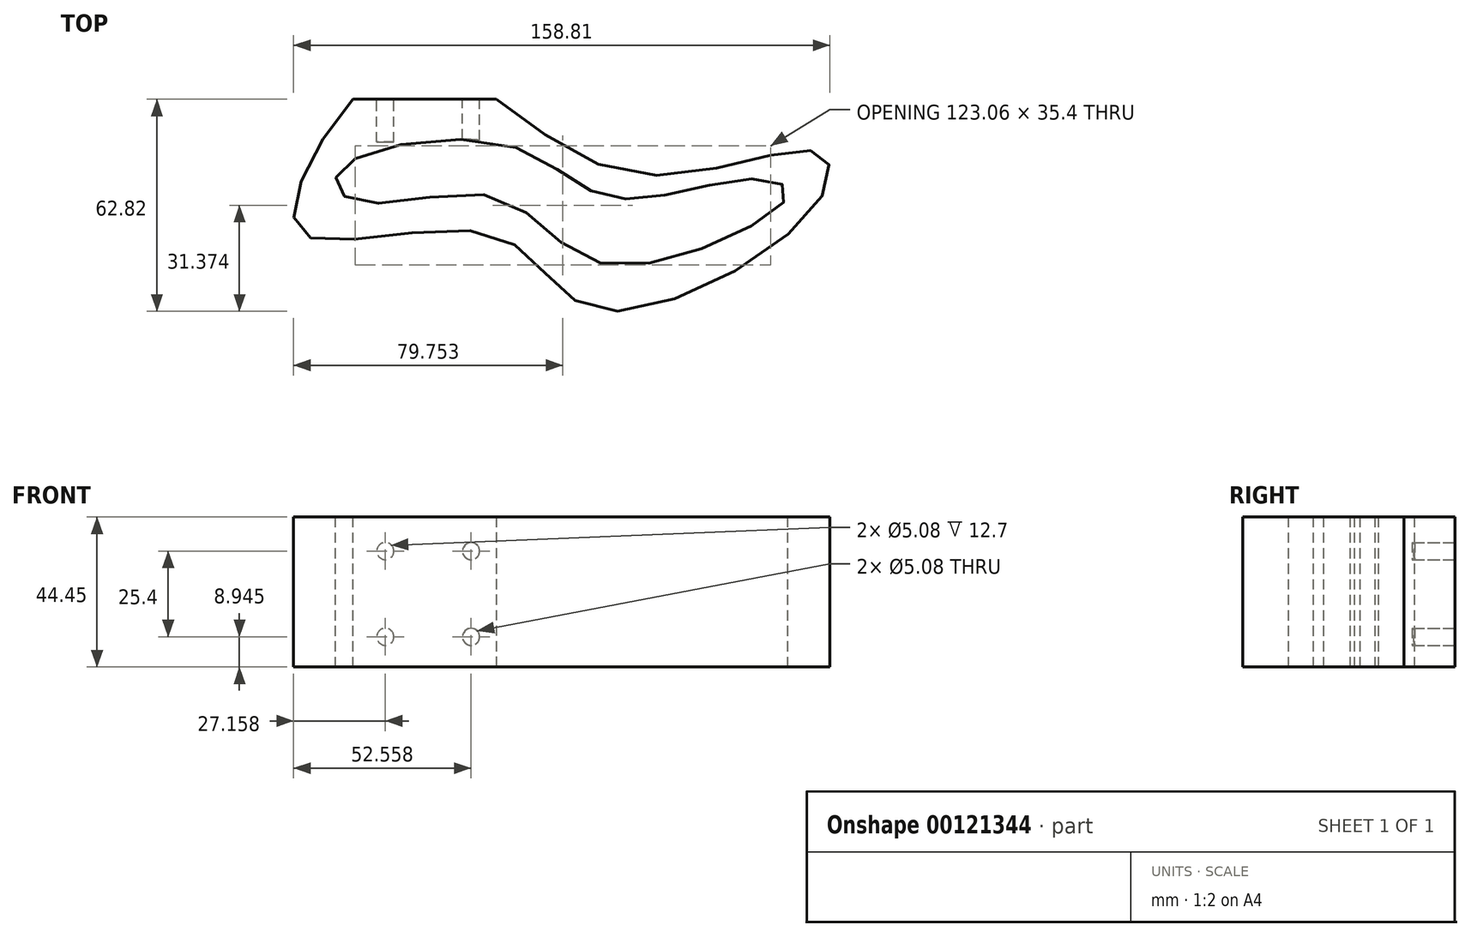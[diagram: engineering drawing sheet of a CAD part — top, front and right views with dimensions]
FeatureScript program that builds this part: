
annotation { "Feature Type Name" : "Feature", "Feature Type Description" : "" }
export const myFeature = defineFeature(function(context is Context, id is Id, definition is map)
    precondition{}
    {
        {
            var Q0;
            Q0=qCreatedBy(makeId("Top.planeOp"),FACE);
            var sketch = newSketch(context, id + "F0", { "sketchPlane" : qUnion([Q0])});
            skFitSpline(sketch, "E0", {"points": [v(-48.63, 41.45) * mm, v(-16.37, 66.66) * mm, v(43, 34.45) * mm, v(99.55, 40.56) * mm, v(99.65, 25.44) * mm, v(34.13, -6.14) * mm, v(4.23, 15.87) * mm, v(-52.44, 15.97) * mm, v(-48.63, 41.45) * mm]});
            skSolve(sketch);
        }
        {
            var Q0;
            Q0 = qSketchRegion(id + "F0", true);
            extrude(context, id + "F1", {"entities" : qUnion([Q0]), "depth" : 44.45 * mm});
        }
        {
            var Q0;
            Q0=makeQuery(id+"F1.opExtrude","CAP_FACE",FACE,{"disambiguationData":[OSD([sQuery(id+"F0.wireOp",EDGE,"E0")])],"isStart":false});
            var sketch = newSketch(context, id + "F2", { "sketchPlane" : qUnion([Q0])});
            skLineSegment(sketch, "E1.bottom", {"start": v(-38.02, 56.19) * mm, "end": v(36.25, 56.19) * mm});
            skLineSegment(sketch, "E1.top", {"start": v(-38.02, 75.37) * mm, "end": v(36.25, 75.37) * mm});
            skLineSegment(sketch, "E1.left", {"start": v(-38.02, 56.19) * mm, "end": v(-38.02, 75.37) * mm});
            skLineSegment(sketch, "E1.right", {"start": v(36.25, 56.19) * mm, "end": v(36.25, 75.37) * mm});
            skSolve(sketch);
        }
        {
            var Q0;
            Q0 = qSketchRegion(id + "F2", true);
            extrude(context, id + "F3", {"entities" : qUnion([Q0]), "operationType" : NewBodyOperationType.REMOVE, "oppositeDirection" : true, "depth" : 44.45 * mm});
        }
        {
            var Q0;
            Q0=makeQuery(id+"F3.boolean.opBoolean","COPY",FACE,{"derivedFrom":makeQuery(id+"F3.opExtrude","SWEPT_FACE",FACE,{"disambiguationData":[OSD([sQuery(id+"F2.wireOp",EDGE,"E1.bottom")])]})});
            var sketch = newSketch(context, id + "F4", { "sketchPlane" : qUnion([Q0])});
            skCircle(sketch, "E2", {"center": v(28.42, 8.95) * mm, "radius": 2.54 * mm});
            skCircle(sketch, "E3.0.1.0", {"center": v(28.42, 34.35) * mm, "radius": 2.54 * mm});
            skCircle(sketch, "E3.1.0.0", {"center": v(3.02, 8.95) * mm, "radius": 2.54 * mm});
            skCircle(sketch, "E3.1.1.0", {"center": v(3.02, 34.35) * mm, "radius": 2.54 * mm});
            skLineSegment(sketch, "E3.direction1", {"start": v(28.42, 8.95) * mm, "end": v(3.02, 8.95) * mm, "construction": true});
            skLineSegment(sketch, "E3.direction2", {"start": v(28.42, 8.95) * mm, "end": v(28.42, 34.35) * mm, "construction": true});
            skSolve(sketch);
        }
        {
            var Q0;
            Q0 = qSketchRegion(id + "F4", true);
            extrude(context, id + "F5", {"entities" : qUnion([Q0]), "operationType" : NewBodyOperationType.REMOVE, "oppositeDirection" : true, "depth" : 12.7 * mm});
        }
        {
            var Q0;
            Q0=makeQuery(id+"F1.opExtrude","CAP_FACE",FACE,{"disambiguationData":[OSD([sQuery(id+"F0.wireOp",EDGE,"E0")])],"isStart":false});
            var sketch = newSketch(context, id + "F6", { "sketchPlane" : qUnion([Q0])});
            skFitSpline(sketch, "E4", {"points": [v(-37.36, 38.55) * mm, v(-43.1, 31.32) * mm, v(-35.33, 25.48) * mm, v(4.6, 27.13) * mm, v(30.78, 9.15) * mm, v(69.98, 13.77) * mm, v(90.77, 28.3) * mm, v(84.2, 32.5) * mm, v(56.1, 28.1) * mm, v(33.88, 28.41) * mm, v(8.14, 42.53) * mm, v(-37.36, 38.55) * mm]});
            skSolve(sketch);
        }
        {
            var Q0;
            Q0 = qSketchRegion(id + "F6", true);
            var Q1;
            Q1=makeQuery(id+"F1.opExtrude","CAP_FACE",FACE,{"disambiguationData":[OSD([sQuery(id+"F0.wireOp",EDGE,"E0")])],"isStart":true});
            extrude(context, id + "F7", {"entities" : qUnion([Q0]), "operationType" : NewBodyOperationType.REMOVE, "endBound" : BoundingType.UP_TO_SURFACE, "oppositeDirection" : true, "endBoundEntityFace" : qUnion([Q1]), "depth" : 25.4 * mm});
        }
    });
